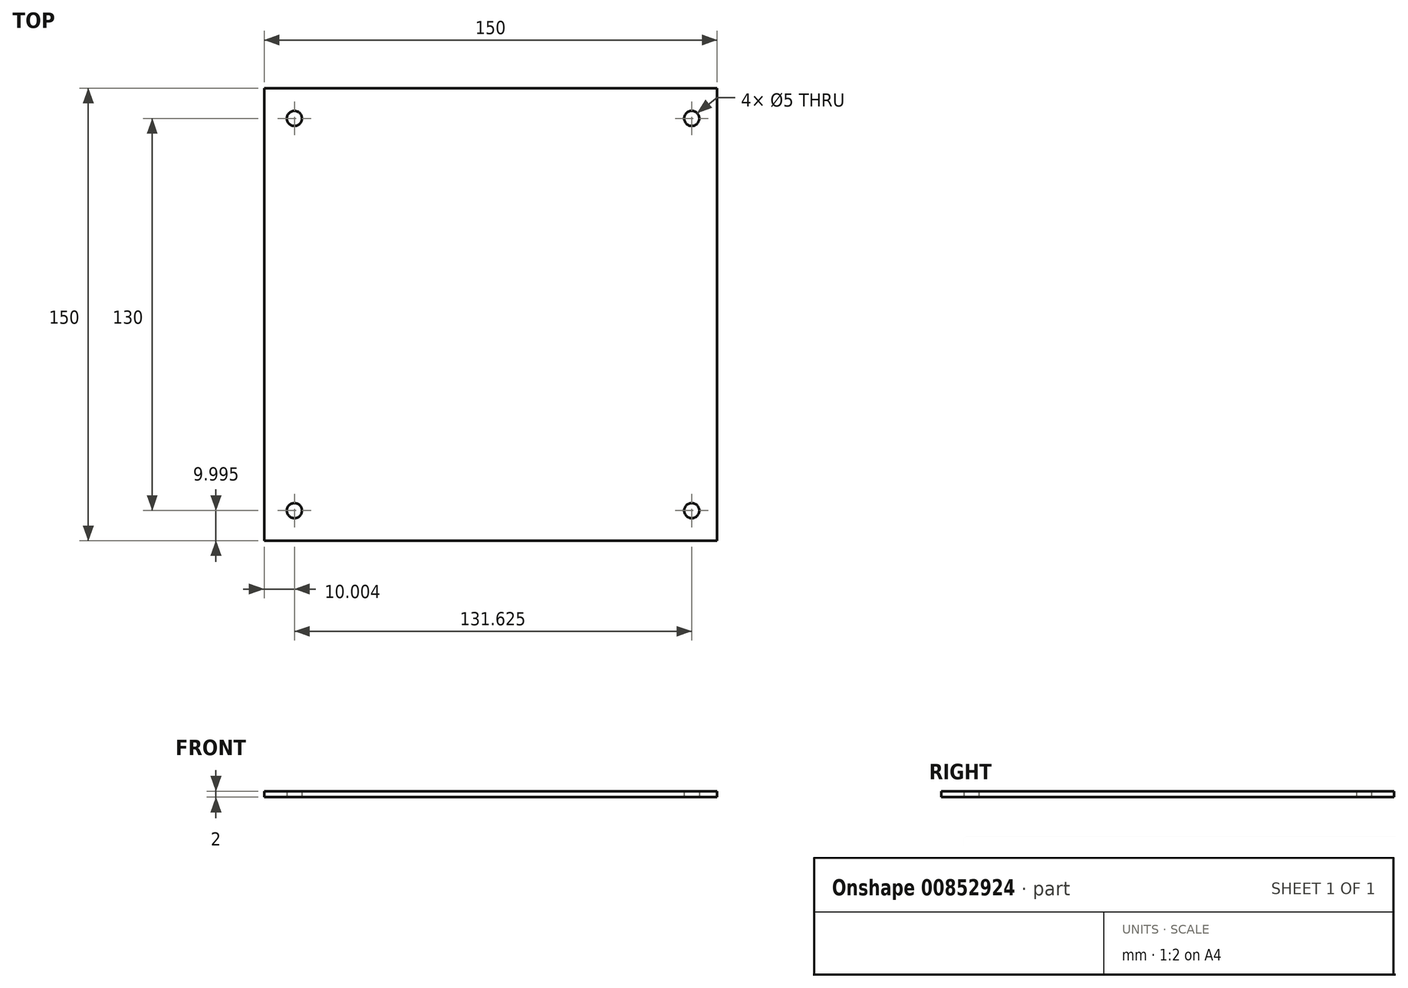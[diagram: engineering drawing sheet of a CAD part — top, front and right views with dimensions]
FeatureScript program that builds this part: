
annotation { "Feature Type Name" : "Feature", "Feature Type Description" : "" }
export const myFeature = defineFeature(function(context is Context, id is Id, definition is map)
    precondition{}
    {
        {
            var Q0;
            Q0=qCreatedBy(makeId("Top.planeOp"),FACE);
            var sketch = newSketch(context, id + "F0", { "sketchPlane" : qUnion([Q0])});
            skCircle(sketch, "E0", {"center": v(-65.05, 64.98) * mm, "radius": 2.5 * mm});
            skCircle(sketch, "E1", {"center": v(66.58, 64.98) * mm, "radius": 2.5 * mm});
            skCircle(sketch, "E2", {"center": v(-65.05, -65.02) * mm, "radius": 2.5 * mm});
            skCircle(sketch, "E3", {"center": v(66.58, -65.02) * mm, "radius": 2.5 * mm});
            skLineSegment(sketch, "E4.bottom", {"start": v(-75.05, 74.98) * mm, "end": v(74.95, 74.98) * mm});
            skLineSegment(sketch, "E4.top", {"start": v(-75.05, -75.02) * mm, "end": v(74.95, -75.02) * mm});
            skLineSegment(sketch, "E4.left", {"start": v(-75.05, 74.98) * mm, "end": v(-75.05, -75.02) * mm});
            skLineSegment(sketch, "E4.right", {"start": v(74.95, 74.98) * mm, "end": v(74.95, -75.02) * mm});
            skSolve(sketch);
        }
        {
            var Q0;
            Q0=makeQuery(id+"F0.imprint","IMPRINT",FACE,{"disambiguationData":[TD([[makeQuery(id+"F0.imprint","IMPRINT",EDGE,{"derivedFrom":sQuery(id+"F0.wireOp",EDGE,"E0")}),-1.0]])]});
            extrude(context, id + "F1", {"entities" : qUnion([Q0]), "depth" : 2 * mm, "offsetDistance" : 25 * mm});
        }
    });
